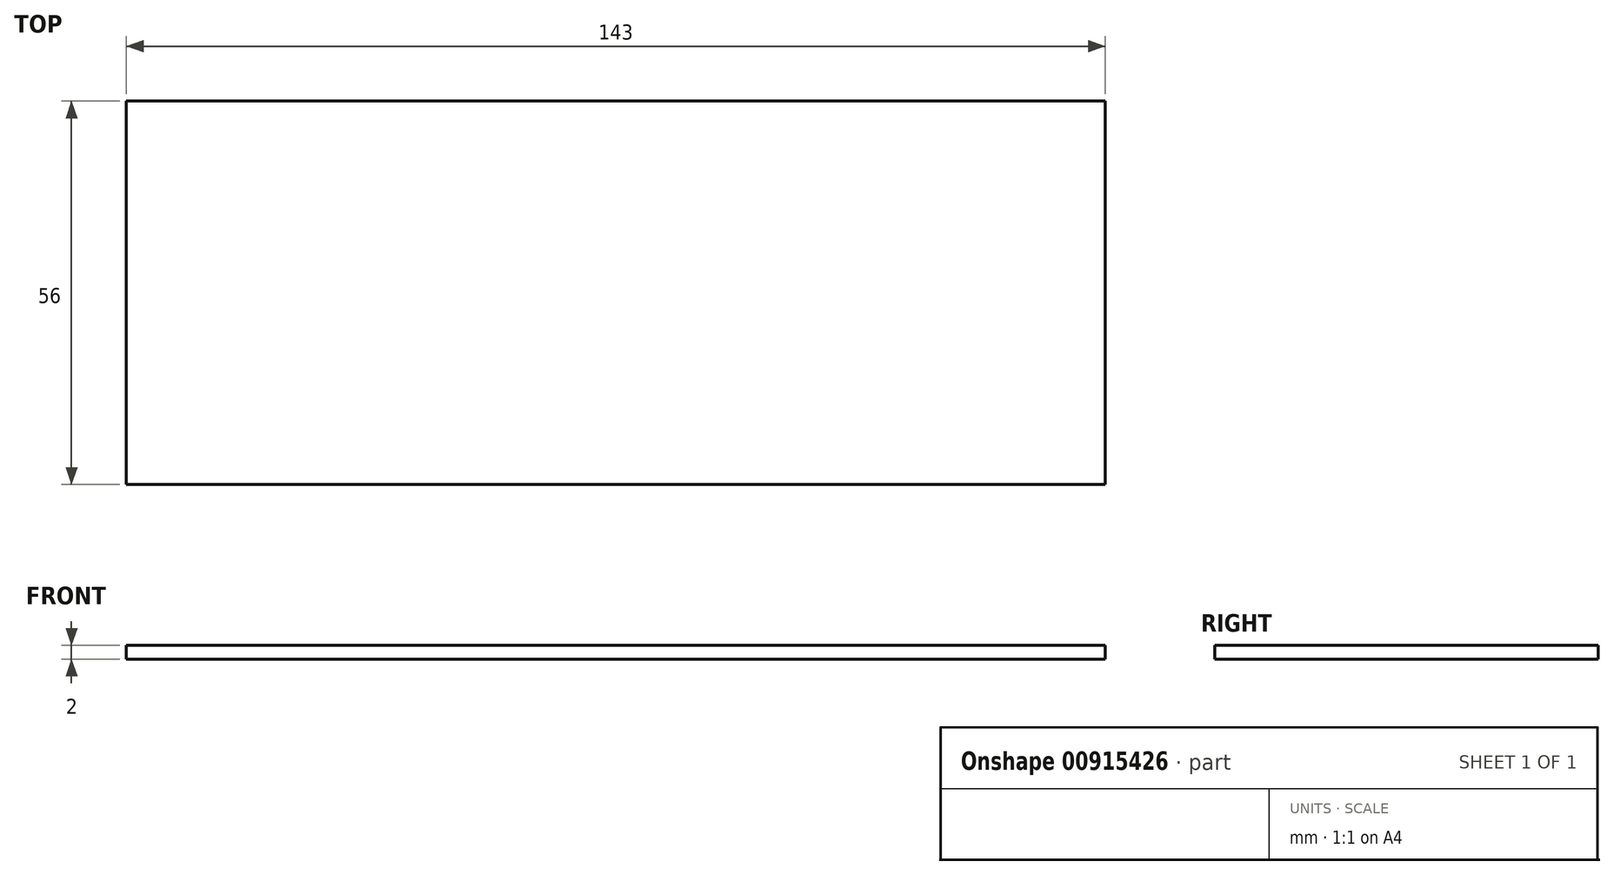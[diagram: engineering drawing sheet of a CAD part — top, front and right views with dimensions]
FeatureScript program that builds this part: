
annotation { "Feature Type Name" : "Feature", "Feature Type Description" : "" }
export const myFeature = defineFeature(function(context is Context, id is Id, definition is map)
    precondition{}
    {
        {
            var Q0;
            Q0=qCreatedBy(makeId("Top.planeOp"),FACE);
            var sketch = newSketch(context, id + "F0", { "sketchPlane" : qUnion([Q0])});
            skLineSegment(sketch, "E0.bottom", {"start": v(0, 0) * mm, "end": v(143, 0) * mm});
            skLineSegment(sketch, "E0.top", {"start": v(0, 56) * mm, "end": v(143, 56) * mm});
            skLineSegment(sketch, "E0.left", {"start": v(0, 0) * mm, "end": v(0, 56) * mm});
            skLineSegment(sketch, "E0.right", {"start": v(143, 0) * mm, "end": v(143, 56) * mm});
            skSolve(sketch);
        }
        {
            var Q0;
            Q0=makeQuery(id+"F0.imprint","IMPRINT",FACE,{"disambiguationData":[TD([[makeQuery(id+"F0.imprint","IMPRINT",EDGE,{"derivedFrom":sQuery(id+"F0.wireOp",EDGE,"E0.bottom")}),1.0]])]});
            extrude(context, id + "F1", {"entities" : qUnion([Q0]), "depth" : 2 * mm, "offsetDistance" : 25 * mm});
        }
        {
            var Q0;
            Q0=makeQuery(id+"F1.opExtrude","SWEPT_FACE",FACE,{"disambiguationData":[OSD([sQuery(id+"F0.wireOp",EDGE,"E0.right")])]});
            var sketch = newSketch(context, id + "F2", { "sketchPlane" : qUnion([Q0])});
            skLineSegment(sketch, "E1", {"start": v(0, 0) * mm, "end": v(56, 0) * mm});
            skSolve(sketch);
        }
        {
            var Q0;
            Q0 = qSketchRegion(id + "F2", true);
            var Q1;
            Q1=sQuery(id+"F2.wireOp",EDGE,"E1");
            var Q2;
            Q2=makeQuery(id+"F1.opExtrude","SWEPT_FACE",FACE,{"disambiguationData":[OSD([sQuery(id+"F0.wireOp",EDGE,"E0.left")])]});
            extrude(context, id + "F3", {"entities" : qUnion([Q0]), "bodyType" : ToolBodyType.SURFACE, "surfaceEntities" : qUnion([Q1]), "endBound" : BoundingType.UP_TO_SURFACE, "oppositeDirection" : true, "depth" : 77.8 * mm, "endBoundEntityFace" : qUnion([Q2]), "offsetDistance" : 25 * mm});
        }
    });
